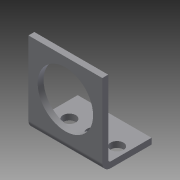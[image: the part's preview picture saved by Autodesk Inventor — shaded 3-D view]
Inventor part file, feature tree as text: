
AUTODESK INVENTOR PART (.ipt)
format: ipt  version: 2013 (Build 170138000, 138)  size: 184,832 bytes
history: native  units: in
note: dims shown in document units (in); Inventor stores cm internally (conversion verified against a paired STEP export)
features: other x7, sketch x5, sheet_metal_op x4, reference x3
ambient origin geometry x8: Origin, YZ Plane, XZ Plane, XY Plane, X Axis, Y Axis, Z Axis, Center Point
bodies: Solid1 (feature_tree)
feature tree (19):
  sheet_metal_op  "Face1"
  sheet_metal_op  "Flange1"
  sketch  "Sketch1"  dims[d0=1.5in]
  other  "Plate1"
  sketch  "Sketch2"  dims[d1=1.5in]
  sketch  "Sketch3"  dims[d2=0.75in]
  other  "Plate2"
  sheet_metal_op  "Bend1"
  sheet_metal_op  "Corner1"
  sketch  "Sketch6"  dims[d3=0.75in]
  reference  "Reference1"
  reference  "Reference2"
  sketch  "Sketch7"  dims[d4=0.12in d7=0.75in d8=1.125in d9=0.12in d10=0.0in d11=0.12in d12=0.06in d13=0.24in d14=0.12in d15=1.0in d16=90.0deg d17=0.05in d18=0.48in d19=0.12in d20=0.12in d28=0.12in d29=0.0in d30=0.12in d31=0.0in d5=0.0in d6=0.0312in]
  reference  "Reference3"
  other  "Cut1"
  other  "Cut3"
  other  "Cut4"
  other  "Definition1"
  other  "Cut2"
